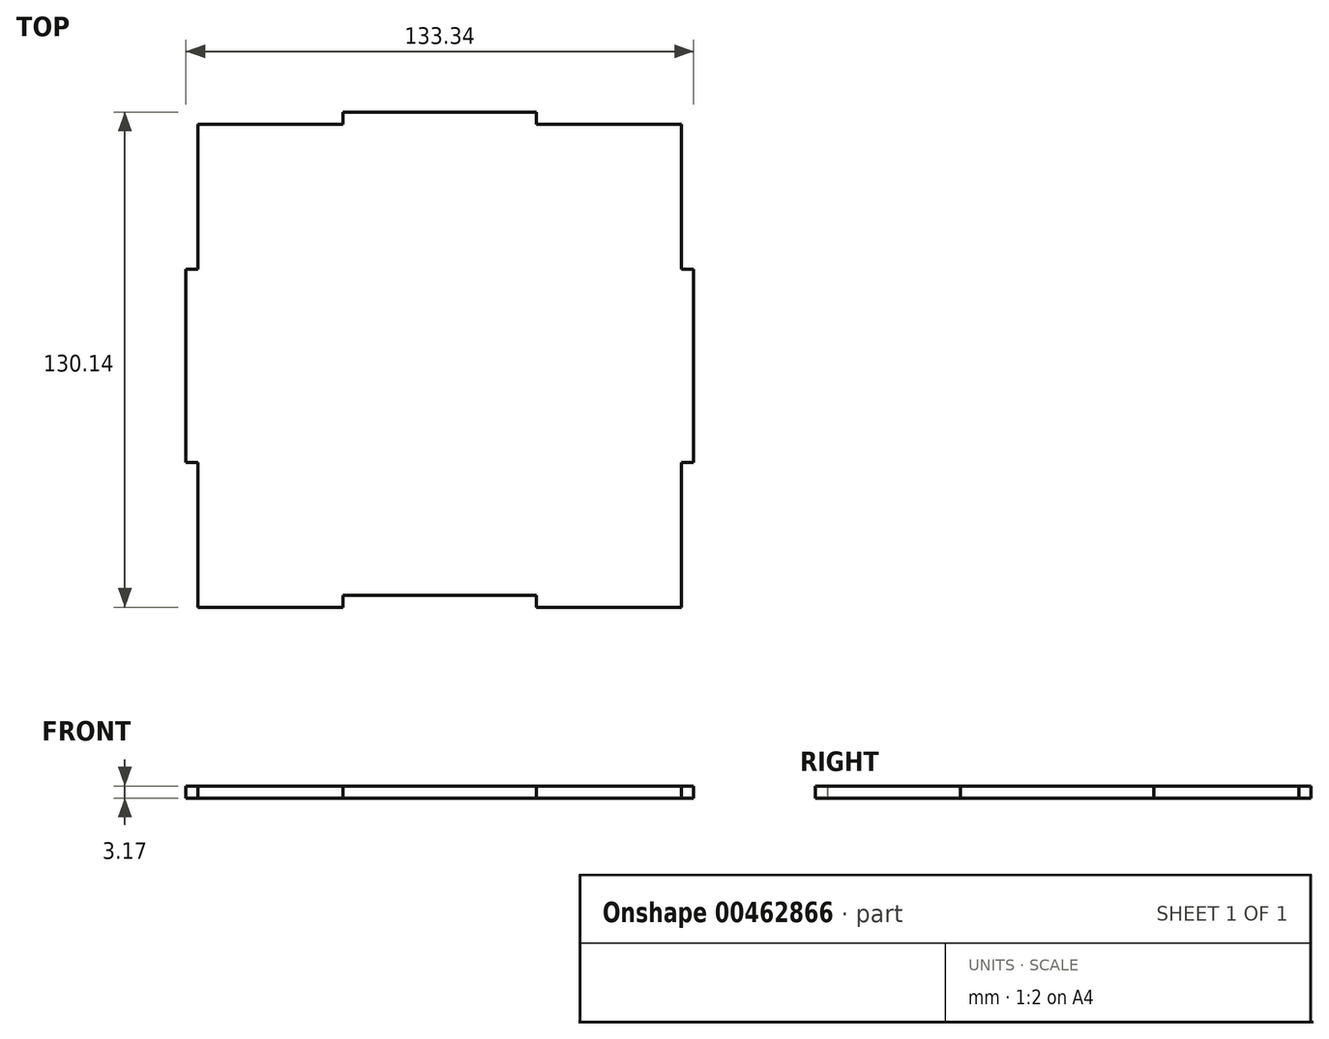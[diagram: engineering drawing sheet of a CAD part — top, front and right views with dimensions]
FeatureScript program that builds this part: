
annotation { "Feature Type Name" : "Feature", "Feature Type Description" : "" }
export const myFeature = defineFeature(function(context is Context, id is Id, definition is map)
    precondition{}
    {
        {
            var Q0;
            Q0=qCreatedBy(makeId("Top.planeOp"),FACE);
            var sketch = newSketch(context, id + "F0", { "sketchPlane" : qUnion([Q0])});
            skLineSegment(sketch, "E0.bottom", {"start": v(63.5, -63.48) * mm, "end": v(25.4, -63.48) * mm});
            skLineSegment(sketch, "E0.top", {"start": v(63.5, 63.48) * mm, "end": v(25.4, 63.48) * mm});
            skLineSegment(sketch, "E0.left", {"start": v(63.5, -63.48) * mm, "end": v(63.5, -25.4) * mm});
            skLineSegment(sketch, "E0.right", {"start": v(-63.5, -63.48) * mm, "end": v(-63.5, -25.4) * mm});
            skPoint(sketch, "E0.middle", {"position": v(0, 0) * mm});
            skLineSegment(sketch, "E1.bottom", {"start": v(66.68, -25.4) * mm, "end": v(63.5, -25.4) * mm});
            skLineSegment(sketch, "E1.top", {"start": v(66.68, 25.4) * mm, "end": v(63.5, 25.4) * mm});
            skLineSegment(sketch, "E1.left", {"start": v(66.67, -25.4) * mm, "end": v(66.67, 25.4) * mm});
            skPoint(sketch, "E1.middle", {"position": v(63.5, 0) * mm});
            skPoint(sketch, "E2.orphan", {"position": v(60.33, -25.4) * mm});
            skPoint(sketch, "E3.orphan", {"position": v(60.32, 25.4) * mm});
            skLineSegment(sketch, "E4.trimOffspring", {"start": v(63.5, 25.4) * mm, "end": v(63.5, 63.48) * mm});
            skPoint(sketch, "E5.middle", {"position": v(-63.5, 0) * mm});
            skPoint(sketch, "E5.left.start.orphan", {"position": v(-60.32, -25.4) * mm});
            skPoint(sketch, "E6.orphan", {"position": v(-60.32, 25.4) * mm});
            skLineSegment(sketch, "E7.trimOffspring", {"start": v(-63.5, 25.4) * mm, "end": v(-63.5, 63.48) * mm});
            skPoint(sketch, "E5.top.end.orphan", {"position": v(-66.67, 25.4) * mm});
            skPoint(sketch, "E5.bottom.end.orphan", {"position": v(-66.67, -25.4) * mm});
            skLineSegment(sketch, "E8.top", {"start": v(25.4, 66.66) * mm, "end": v(-25.4, 66.66) * mm});
            skLineSegment(sketch, "E8.left", {"start": v(25.4, 63.48) * mm, "end": v(25.4, 66.66) * mm});
            skLineSegment(sketch, "E8.right", {"start": v(-25.4, 63.48) * mm, "end": v(-25.4, 66.66) * mm});
            skPoint(sketch, "E8.middle", {"position": v(0, 63.48) * mm});
            skLineSegment(sketch, "E9.trimOffspring", {"start": v(-25.4, 63.48) * mm, "end": v(-63.5, 63.48) * mm});
            skPoint(sketch, "E8.bottom.end.orphan", {"position": v(-25.4, 60.3) * mm});
            skPoint(sketch, "E8.bottom.start.orphan", {"position": v(25.4, 60.3) * mm});
            skLineSegment(sketch, "E10.bottom", {"start": v(25.4, -60.3) * mm, "end": v(-25.4, -60.3) * mm});
            skLineSegment(sketch, "E10.left", {"start": v(25.4, -60.3) * mm, "end": v(25.4, -63.48) * mm});
            skLineSegment(sketch, "E10.right", {"start": v(-25.4, -60.3) * mm, "end": v(-25.4, -63.48) * mm});
            skPoint(sketch, "E10.middle", {"position": v(0, -63.48) * mm});
            skLineSegment(sketch, "E11.trimOffspring", {"start": v(-25.4, -63.48) * mm, "end": v(-63.5, -63.48) * mm});
            skPoint(sketch, "E12.orphan", {"position": v(-25.4, -66.66) * mm});
            skPoint(sketch, "E13.orphan", {"position": v(25.4, -66.66) * mm});
            skLineSegment(sketch, "E14", {"start": v(-63.5, -25.4) * mm, "end": v(-66.67, -25.4) * mm});
            skLineSegment(sketch, "E15", {"start": v(-66.67, 25.4) * mm, "end": v(-66.67, -25.4) * mm});
            skLineSegment(sketch, "E16", {"start": v(-66.67, 25.4) * mm, "end": v(-63.5, 25.4) * mm});
            skSolve(sketch);
        }
        {
            var Q0;
            Q0 = qSketchRegion(id + "F0", true);
            extrude(context, id + "F1", {"entities" : qUnion([Q0]), "depth" : 3.17 * mm});
        }
    });
